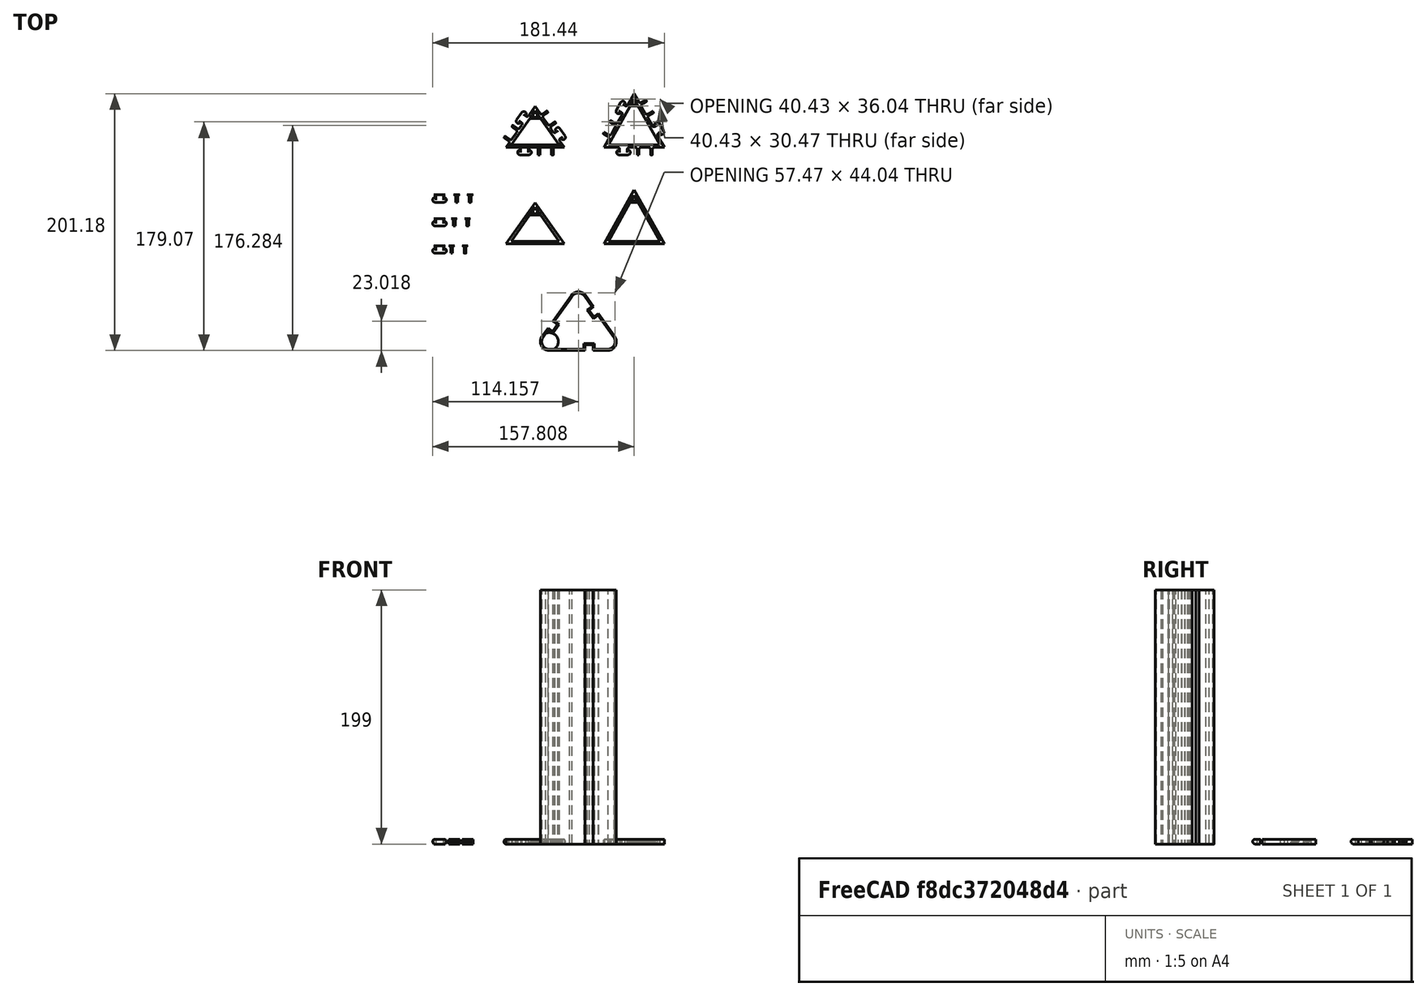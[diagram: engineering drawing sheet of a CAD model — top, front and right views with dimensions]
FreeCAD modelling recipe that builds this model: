
FCSTD DOCUMENT  (FreeCAD 0.20R29177 +233 (Git))
Label: NewGeodesicDome
License: All rights reserved
LicenseURL: http://en.wikipedia.org/wiki/All_rights_reserved
objects: Part::Part2DObjectPython×65, Part::Feature×30, Part::Extrusion×7, Part::MultiFuse×6, Part::Refine×6, Part::Cut×4, Part::FeaturePython×3, App::DocumentObjectGroup×2
note: 121 computed .brp shape members not serialized (recipe doc carries the construction recipe); baked Part::Feature solids carry a one-line shape summary decoded from their .brp

FEATURE [Part::Part2DObjectPython] Line183  label="Line184"  # Draft 2D object (typed FeaturePython)
  ChamferSize = 0
  Closed = false
  End = (88.7449,0.299498,-125.386)
  FilletRadius = 0
  Length = 60.5325
  MakeFace = true
  Placement = pos=(28.2124,0.299498,-125.386) rot=(0,0,1;3.14159rad)
  Points = (2) [(0,0,0),(-60.5325,0,0)]
  Start = (28.2124,0.299498,-125.386)
  Subdivisions = 0
FEATURE [Part::Part2DObjectPython] Line225  label="Line226"  # Draft 2D object (typed FeaturePython)
  ChamferSize = 0
  Closed = false
  End = (58.4771,54.2505,-125.386)
  FilletRadius = 0
  Length = 61.8615
  MakeFace = true
  Placement = pos=(88.7449,0.299498,-125.386) rot=(0,0,1;3.14159rad)
  Points = (2) [(0,0,0),(30.2678,-53.951,0)]
  Start = (88.7449,0.299498,-125.386)
  Subdivisions = 0
FEATURE [Part::Part2DObjectPython] Line175  label="Line186"  # Draft 2D object (typed FeaturePython)
  ChamferSize = 0
  Closed = false
  End = (58.4778,54.2518,-125.386)
  FilletRadius = 0
  Length = 61.8615
  MakeFace = true
  Placement = pos=(28.2124,0.299498,-125.386) rot=(0,0,1;3.14159rad)
  Points = (2) [(0,0,0),(-30.2655,-53.9523,0)]
  Start = (28.2124,0.299498,-125.386)
  Subdivisions = 0
FEATURE [Part::Feature] Cut011001001  label="base-6"
  shape: bbox 47.27 x 42.13 x 3.8 mm, 9 faces (baked)
FEATURE [Part::Part2DObjectPython] Line219  label="Line220"  # Draft 2D object (typed FeaturePython)
  ChamferSize = 0
  Closed = false
  End = (11.2032,0.299498,-125.386)
  FilletRadius = 0
  Length = 52.293
  MakeFace = true
  Placement = pos=(-19.0727,42.9367,-125.386) rot=(0,0,1;3.14159rad)
  Points = (2) [(0,0,0),(-30.2758,42.6372,0)]
  Start = (-19.0727,42.9367,-125.386)
  Subdivisions = 0
FEATURE [Part::Part2DObjectPython] Line217  label="Line218"  # Draft 2D object (typed FeaturePython)
  ChamferSize = 0
  Closed = false
  End = (11.2032,0.299498,-125.386)
  FilletRadius = 0
  Length = 60.5325
  MakeFace = true
  Placement = pos=(-49.3293,0.299498,-125.386) rot=(0,0,1;3.14159rad)
  Points = (2) [(0,0,0),(-60.5325,0,0)]
  Start = (-49.3293,0.299498,-125.386)
  Subdivisions = 0
FEATURE [Part::Part2DObjectPython] Line218  label="Line219"  # Draft 2D object (typed FeaturePython)
  ChamferSize = 0
  Closed = false
  End = (-19.0639,42.9441,-125.386)
  FilletRadius = 0
  Length = 52.293
  MakeFace = true
  Placement = pos=(-49.3293,0.299498,-125.386) rot=(0,0,1;3.14159rad)
  Points = (2) [(0,0,0),(-30.2654,-42.6446,0)]
  Start = (-49.3293,0.299498,-125.386)
  Subdivisions = 0
FEATURE [Part::Feature] Cut011001002001001  label="Base-5"
  shape: bbox 45.49 x 32.04 x 3.8 mm, 9 faces (baked)
FEATURE [Part::Feature] Fusion002009002005002004028003007012002018_solid001001  label="Connector-Father"
  Placement = pos=(-29.7814,0,0) rot=(0,0,1;0rad)
  shape: bbox 10.8 x 5.785 x 3.8 mm, 11 faces (baked)
FEATURE [Part::Feature] Fusion002009002005002004028003007012002019001001  label="Connector-Mother"
  Placement = pos=(-25.7814,0,0) rot=(0,0,1;0rad)
  shape: bbox 15 x 5.785 x 3.8 mm, 19 faces, 2 solids (baked)
FEATURE [Part::Part2DObjectPython] Polygon  # Draft 2D object (typed FeaturePython)
  Area = 9.80568
  ChamferSize = 0
  DrawMode = 0
  FacesNumber = 5
  FilletRadius = 0
  MakeFace = true
  Placement = pos=(-19.0701,29.4211,-127.286) rot=(0.987688,0.156434,0;3.14159rad)
  Radius = 2.03079
FEATURE [Part::Extrusion] Extrusion
  Base = -> Polygon
  Dir = (2.39e-14,-6.7e-14,18.2647)
  DirMode = 0
  FaceMakerClass = Part::FaceMakerBullseye
  LengthFwd = 0
  LengthRev = 0
  Solid = true
  Symmetric = false
FEATURE [Part::Part2DObjectPython] Wire  # Draft 2D object (typed FeaturePython)
  Area = 23.5885
  ChamferSize = 0
  Closed = true
  End = (-17.9137,31.14,-127.286)
  FilletRadius = 0
  Length = 21.5142
  MakeFace = true
  Placement = pos=(-14.8164,26.7782,-127.286) rot=(1,0,0;3.14159rad)
  Points = (4) [(0,0,0),(-8.50437,-3.55271e-15,-1.42109e-14),(-5.40871,-4.36186,0),(-3.09727,-4.36187,7.10543e-14)]
  Start = (-14.8164,26.7782,-127.286)
  Subdivisions = 0
FEATURE [Part::Extrusion] Extrusion001
  Base = -> Wire
  Dir = (6.9e-15,5.4e-15,1.9)
  DirMode = 0
  FaceMakerClass = Part::FaceMakerBullseye
  LengthFwd = 0
  LengthRev = 0
  Solid = true
  Symmetric = false
FEATURE [Part::Part2DObjectPython] Wire001  # Draft 2D object (typed FeaturePython)
  Area = 1.88151
  ChamferSize = 0
  Closed = true
  End = (-17.9137,31.14,-123.486)
  FilletRadius = 0
  Length = 6.30447
  MakeFace = true
  Placement = pos=(-20.2251,31.14,-123.486) rot=(0,0,1;0rad)
  Points = (3) [(0,0,0),(1.15542,1.62801,1.42109e-14),(2.31143,1.92071e-07,-2.84217e-14)]
  Start = (-20.2251,31.14,-123.486)
  Subdivisions = 0
FEATURE [Part::Extrusion] Extrusion002
  Base = -> Wire001
  Dir = (-2.59e-14,4.01e-14,-1.9)
  DirMode = 0
  FaceMakerClass = Part::FaceMakerBullseye
  LengthFwd = 0
  LengthRev = 0
  Solid = true
  Symmetric = false
FEATURE [Part::Cut] Cut
  Base = -> Cut011001002001001
  Tool = -> Extrusion002
FEATURE [Part::MultiFuse] Fusion
  Shapes = -> [Extrusion001,Cut]
FEATURE [Part::Cut] Cut011001002001002
  Base = -> Fusion
  Tool = -> Extrusion
FEATURE [Part::Part2DObjectPython] Polygon002  # Draft 2D object (typed FeaturePython)
  Area = 7.50844
  ChamferSize = 0
  DrawMode = 0
  FacesNumber = 6
  FilletRadius = 0
  MakeFace = true
  Placement = pos=(58.4772,39.1234,-127.286) rot=(1,0,0;3.14159rad)
  Radius = 1.7
FEATURE [Part::Part2DObjectPython] Wire002  # Draft 2D object (typed FeaturePython)
  Area = 1.48683
  ChamferSize = 0
  Closed = true
  End = (59.3905,40.5956,-123.486)
  FilletRadius = 0
  Length = 5.55993
  MakeFace = true
  Placement = pos=(57.564,40.5956,-123.486) rot=(0,0,1;0rad)
  Points = (3) [(0,0,0),(0.913226,1.62801,0),(1.82657,1.51781e-07,0)]
  Start = (57.564,40.5956,-123.486)
  Subdivisions = 0
FEATURE [Part::Extrusion] Extrusion003
  Base = -> Wire002
  Dir = (4e-16,-8e-16,-1.9)
  DirMode = 0
  FaceMakerClass = Part::FaceMakerBullseye
  LengthFwd = 0
  LengthRev = 0
  Solid = true
  Symmetric = false
FEATURE [Part::Cut] Cut011001002001003
  Base = -> Cut011001001
  Tool = -> Extrusion003
FEATURE [Part::Part2DObjectPython] Wire003  # Draft 2D object (typed FeaturePython)
  Area = 15.9332
  ChamferSize = 0
  Closed = true
  End = (55.3513,36.6511,-127.286)
  FilletRadius = 0
  Length = 17.1242
  MakeFace = true
  Placement = pos=(61.6035,36.6511,-127.286) rot=(1,0,0;3.14159rad)
  Points = (4) [(0,0,0),(-2.21293,-3.94449,0),(-4.0395,-3.94449,0),(-6.25215,0,2.84217e-14)]
  Start = (61.6035,36.6511,-127.286)
  Subdivisions = 0
FEATURE [Part::Extrusion] Extrusion004
  Base = -> Wire003
  Dir = (-8.6e-15,-6e-15,1.9)
  DirMode = 0
  FaceMakerClass = Part::FaceMakerBullseye
  LengthFwd = 0
  LengthRev = 0
  Solid = true
  Symmetric = false
FEATURE [Part::Extrusion] Extrusion005
  Base = -> Polygon002
  Dir = (-3.4e-15,6.6e-15,15.6059)
  DirMode = 0
  FaceMakerClass = Part::FaceMakerBullseye
  LengthFwd = 0
  LengthRev = 0
  Solid = true
  Symmetric = false
FEATURE [Part::Cut] Cut011001002001004
  Base = -> Extrusion004
  Tool = -> Extrusion005
FEATURE [Part::MultiFuse] Fusion002009002005002004028003007012002019001002
  Shapes = -> [Cut011001002001004,Cut011001002001003]
FEATURE [Part::Refine] Fusion002009002005002004028003007012002019001002001
  Source = -> Fusion002009002005002004028003007012002019001002
FEATURE [Part::Refine] Cut011001002001002001
  Source = -> Cut011001002001002
FEATURE [Part::Feature] Cut011001002001002001001  label="Base-5angel"
  shape: bbox 45.49 x 32.04 x 3.8 mm, 17 faces (baked)
FEATURE [Part::Feature] Fusion002009002005002004028003007012002019001002001001  label="Base-6angel"
  shape: bbox 47.27 x 42.13 x 3.8 mm, 16 faces (baked)
FEATURE [Part::Part2DObjectPython] Line270  label="Line271"  # Draft 2D object (typed FeaturePython)
  ChamferSize = 0
  Closed = false
  End = (58.4771,129.656,-125.386)
  FilletRadius = 0
  Length = 61.8615
  MakeFace = true
  Placement = pos=(88.7449,75.7054,-125.386) rot=(0,0,1;3.14159rad)
  Points = (2) [(0,0,0),(30.2678,-53.951,0)]
  Start = (88.7449,75.7054,-125.386)
  Subdivisions = 0
FEATURE [Part::Part2DObjectPython] Line271  label="Line272"  # Draft 2D object (typed FeaturePython)
  ChamferSize = 0
  Closed = false
  End = (58.4778,129.658,-125.386)
  FilletRadius = 0
  Length = 61.8615
  MakeFace = true
  Placement = pos=(28.2124,75.7054,-125.386) rot=(0,0,1;3.14159rad)
  Points = (2) [(0,0,0),(-30.2655,-53.9523,0)]
  Start = (28.2124,75.7054,-125.386)
  Subdivisions = 0
FEATURE [Part::Part2DObjectPython] Line272  label="Line273"  # Draft 2D object (typed FeaturePython)
  ChamferSize = 0
  Closed = false
  End = (88.7449,75.7054,-125.386)
  FilletRadius = 0
  Length = 60.5325
  MakeFace = true
  Placement = pos=(28.2124,75.7054,-125.386) rot=(0,0,1;3.14159rad)
  Points = (2) [(0,0,0),(-60.5325,0,0)]
  Start = (28.2124,75.7054,-125.386)
  Subdivisions = 0
FEATURE [Part::Part2DObjectPython] Line273  label="Line274"  # Draft 2D object (typed FeaturePython)
  ChamferSize = 0
  Closed = false
  End = (11.2032,75.7054,-125.386)
  FilletRadius = 0
  Length = 60.5325
  MakeFace = true
  Placement = pos=(-49.3293,75.7054,-125.386) rot=(0,0,1;3.14159rad)
  Points = (2) [(0,0,0),(-60.5325,0,0)]
  Start = (-49.3293,75.7054,-125.386)
  Subdivisions = 0
FEATURE [Part::Part2DObjectPython] Line274  label="Line275"  # Draft 2D object (typed FeaturePython)
  ChamferSize = 0
  Closed = false
  End = (11.2032,75.7054,-125.386)
  FilletRadius = 0
  Length = 52.293
  MakeFace = true
  Placement = pos=(-19.0727,118.343,-125.386) rot=(0,0,1;3.14159rad)
  Points = (2) [(0,0,0),(-30.2758,42.6372,0)]
  Start = (-19.0727,118.343,-125.386)
  Subdivisions = 0
FEATURE [Part::Part2DObjectPython] Line275  label="Line276"  # Draft 2D object (typed FeaturePython)
  ChamferSize = 0
  Closed = false
  End = (-19.0639,118.35,-125.386)
  FilletRadius = 0
  Length = 52.293
  MakeFace = true
  Placement = pos=(-49.3293,75.7054,-125.386) rot=(0,0,1;3.14159rad)
  Points = (2) [(0,0,0),(-30.2654,-42.6446,0)]
  Start = (-49.3293,75.7054,-125.386)
  Subdivisions = 0
FEATURE [Part::Feature] Fusion002009002005002004028003007012002019001002001002  label="Base-6angel001"
  Placement = pos=(0,75.4059,-2.8e-14) rot=(0,0,1;0rad)
  shape: bbox 47.27 x 42.13 x 3.8 mm, 16 faces (baked)
FEATURE [Part::Feature] Cut011001002001002001002  label="Base-5angel001"
  Placement = pos=(0,75.4059,-2.8e-14) rot=(0,0,1;0rad)
  shape: bbox 45.49 x 32.04 x 3.8 mm, 17 faces (baked)
FEATURE [Part::Part2DObjectPython] Line276  label="Line277"  # Draft 2D object (typed FeaturePython)
  Area = 0
  ChamferSize = 0
  Closed = false
  End = (-75.2318,29.5332,-125.386)
  FilletRadius = 0
  Length = 9.03897
  MakeFace = true
  Placement = pos=(-75.2318,38.5722,-125.386) rot=(1,0,0;3.14159rad)
  Points = (2) [(0,0,0),(0,9.03897,0)]
  Start = (-75.2318,38.5722,-125.386)
  Subdivisions = 0
FEATURE [Part::Part2DObjectPython] Line277  label="Line278"  # Draft 2D object (typed FeaturePython)
  Area = 0
  ChamferSize = 0
  Closed = false
  End = (-93.9318,29.5332,-125.386)
  FilletRadius = 0
  Length = 8.13178
  MakeFace = true
  Placement = pos=(-93.9318,37.665,-125.386) rot=(1,0,0;3.14159rad)
  Points = (2) [(0,0,0),(0,8.13178,0)]
  Start = (-93.9318,37.665,-125.386)
  Subdivisions = 0
FEATURE [Part::Part2DObjectPython] Line278  label="Line279"  # Draft 2D object (typed FeaturePython)
  Area = 0
  ChamferSize = 0
  Closed = false
  End = (-104.082,38.5722,-125.386)
  FilletRadius = 0
  Length = 35
  MakeFace = true
  Placement = pos=(-69.0818,38.5722,-125.386) rot=(1,0,0;3.14159rad)
  Points = (2) [(0,0,0),(-35,0,0)]
  Start = (-69.0818,38.5722,-125.386)
  Subdivisions = 0
FEATURE [Part::Part2DObjectPython] Line279  label="Line280"  # Draft 2D object (typed FeaturePython)
  Area = 0
  ChamferSize = 0
  Closed = false
  End = (-84.5818,42.4571,-125.386)
  FilletRadius = 0
  Length = 12.9238
  MakeFace = true
  Placement = pos=(-84.5818,29.5332,-125.386) rot=(1,0,0;3.14159rad)
  Points = (2) [(0,0,0),(8.10019e-13,-12.9238,-1.42109e-14)]
  Start = (-84.5818,29.5332,-125.386)
  Subdivisions = 0
FEATURE [Part::Feature] Fusion002009002005002004028003007012002018_solid001002  label="Connector-Father001"
  Placement = pos=(-29.7814,-18.5719,0) rot=(0,0,1;0rad)
  shape: bbox 10.8 x 5.785 x 3.8 mm, 11 faces (baked)
FEATURE [Part::Feature] Fusion002009002005002004028003007012002019001002001003  label="Connector-Mother001"
  Placement = pos=(-27.7814,-18.5719,0) rot=(0,0,1;0rad)
  shape: bbox 15 x 5.785 x 3.8 mm, 19 faces, 2 solids (baked)
FEATURE [Part::Part2DObjectPython] Line280  label="Line281"  # Draft 2D object (typed FeaturePython)
  Area = 0
  ChamferSize = 0
  Closed = false
  End = (-77.2318,10.9613,-125.386)
  FilletRadius = 0
  Length = 9.03897
  MakeFace = true
  Placement = pos=(-77.2318,20.0003,-125.386) rot=(1,0,0;3.14159rad)
  Points = (2) [(0,0,0),(0,9.03897,0)]
  Start = (-77.2318,20.0003,-125.386)
  Subdivisions = 0
FEATURE [Part::Part2DObjectPython] Line281  label="Line282"  # Draft 2D object (typed FeaturePython)
  Area = 0
  ChamferSize = 0
  Closed = false
  End = (-93.9318,10.9613,-125.386)
  FilletRadius = 0
  Length = 8.13178
  MakeFace = true
  Placement = pos=(-93.9318,19.0931,-125.386) rot=(1,0,0;3.14159rad)
  Points = (2) [(0,0,0),(0,8.13178,0)]
  Start = (-93.9318,19.0931,-125.386)
  Subdivisions = 0
FEATURE [Part::Part2DObjectPython] Line282  label="Line283"  # Draft 2D object (typed FeaturePython)
  Area = 0
  ChamferSize = 0
  Closed = false
  End = (-104.082,20.0003,-125.386)
  FilletRadius = 0
  Length = 35
  MakeFace = true
  Placement = pos=(-69.0818,20.0003,-125.386) rot=(1,0,0;3.14159rad)
  Points = (2) [(0,0,0),(-35,0,0)]
  Start = (-69.0818,20.0003,-125.386)
  Subdivisions = 0
FEATURE [Part::Part2DObjectPython] Line283  label="Line284"  # Draft 2D object (typed FeaturePython)
  Area = 0
  ChamferSize = 0
  Closed = false
  End = (-85.5818,23.8851,-125.386)
  FilletRadius = 0
  Length = 12.9238
  MakeFace = true
  Placement = pos=(-85.5818,10.9613,-125.386) rot=(1,0,0;3.14159rad)
  Points = (2) [(0,0,0),(8.10019e-13,-12.9238,-1.42109e-14)]
  Start = (-85.5818,10.9613,-125.386)
  Subdivisions = 0
FEATURE [Part::Feature] Fusion002009002005002004028003007012002018_solid001003  label="Connector-Father002"
  Placement = pos=(-29.7814,-39.9,0) rot=(0,0,1;0rad)
  shape: bbox 10.8 x 5.785 x 3.8 mm, 11 faces (baked)
FEATURE [Part::Feature] Fusion002009002005002004028003007012002019001002001004  label="Connector-Mother002"
  Placement = pos=(-29.7814,-39.9,0) rot=(0,0,1;0rad)
  shape: bbox 15 x 5.785 x 3.8 mm, 19 faces, 2 solids (baked)
FEATURE [Part::Part2DObjectPython] Line285  label="Line286"  # Draft 2D object (typed FeaturePython)
  Area = 0
  ChamferSize = 0
  Closed = false
  End = (-79.2318,-10.3668,-125.386)
  FilletRadius = 0
  Length = 9.03897
  MakeFace = true
  Placement = pos=(-79.2318,-1.32783,-125.386) rot=(1,0,0;3.14159rad)
  Points = (2) [(0,0,0),(0,9.03897,0)]
  Start = (-79.2318,-1.32783,-125.386)
  Subdivisions = 0
FEATURE [Part::Part2DObjectPython] Line286  label="Line287"  # Draft 2D object (typed FeaturePython)
  Area = 0
  ChamferSize = 0
  Closed = false
  End = (-93.9318,-10.3668,-125.386)
  FilletRadius = 0
  Length = 8.13178
  MakeFace = true
  Placement = pos=(-93.9318,-2.23501,-125.386) rot=(1,0,0;3.14159rad)
  Points = (2) [(0,0,0),(0,8.13178,0)]
  Start = (-93.9318,-2.23501,-125.386)
  Subdivisions = 0
FEATURE [Part::Part2DObjectPython] Line287  label="Line288"  # Draft 2D object (typed FeaturePython)
  Area = 0
  ChamferSize = 0
  Closed = false
  End = (-104.082,-1.32783,-125.386)
  FilletRadius = 0
  Length = 35
  MakeFace = true
  Placement = pos=(-69.0818,-1.32783,-125.386) rot=(1,0,0;3.14159rad)
  Points = (2) [(0,0,0),(-35,0,0)]
  Start = (-69.0818,-1.32783,-125.386)
  Subdivisions = 0
FEATURE [Part::Part2DObjectPython] Line288  label="Line289"  # Draft 2D object (typed FeaturePython)
  Area = 0
  ChamferSize = 0
  Closed = false
  End = (-86.5818,2.55704,-125.386)
  FilletRadius = 0
  Length = 12.9238
  MakeFace = true
  Placement = pos=(-86.5818,-10.3668,-125.386) rot=(1,0,0;3.14159rad)
  Points = (2) [(0,0,0),(8.10019e-13,-12.9238,-1.42109e-14)]
  Start = (-86.5818,-10.3668,-125.386)
  Subdivisions = 0
FEATURE [Part::Part2DObjectPython] Line  # Draft 2D object (typed FeaturePython)
  Area = 0
  ChamferSize = 0
  Closed = false
  End = (-80.2318,23.8851,-127.286)
  FilletRadius = 0
  Length = 2
  MakeFace = true
  Placement = pos=(-82.2318,23.8851,-127.286) rot=(1,0,0;3.14159rad)
  Points = (2) [(0,0,0),(2,0,0)]
  Start = (-82.2318,23.8851,-127.286)
  Subdivisions = 0
FEATURE [Part::Feature] Fusion002009002005002004028003007012002018_solid001004  label="Connector-Father003"
  Placement = pos=(-98.5261,73.0316,-2.42e-13) rot=(0,0,1;4.09518rad)
  shape: bbox 9.698 x 10.67 x 3.8 mm, 11 faces (baked)
FEATURE [Part::Feature] Fusion002009002005002004028003007012002019001002001005  label="Connector-Mother003"
  Placement = pos=(-98.5261,73.0316,-2.42e-13) rot=(0,0,1;4.09518rad)
  shape: bbox 12.53 x 14.36 x 3.8 mm, 19 faces, 2 solids (baked)
FEATURE [Part::Part2DObjectPython] Line291  label="Line292"  # Draft 2D object (typed FeaturePython)
  Area = 0
  ChamferSize = 0
  Closed = false
  End = (-24.0682,111.299,-125.386)
  FilletRadius = 0
  Length = 35
  MakeFace = true
  Placement = pos=(-44.325,82.7566,-125.386) rot=(-0.45893,0.888472,0;3.14159rad)
  Points = (2) [(0,0,0),(-35,1.13687e-13,0)]
  Start = (-44.325,82.7566,-125.386)
  Subdivisions = 0
FEATURE [Part::Part2DObjectPython] Line292  label="Line293"  # Draft 2D object (typed FeaturePython)
  Area = 0
  ChamferSize = 0
  Closed = false
  End = (-37.3139,108.253,-125.386)
  FilletRadius = 0
  Length = 8.13178
  MakeFace = true
  Placement = pos=(-30.6825,103.547,-125.386) rot=(-0.45893,0.888472,0;3.14159rad)
  Points = (2) [(0,0,0),(5.68434e-14,8.13178,0)]
  Start = (-30.6825,103.547,-125.386)
  Subdivisions = 0
FEATURE [Part::Part2DObjectPython] Line293  label="Line294"  # Draft 2D object (typed FeaturePython)
  Area = 0
  ChamferSize = 0
  Closed = false
  End = (-31.0286,94.7793,-125.386)
  FilletRadius = 0
  Length = 12.9238
  MakeFace = true
  Placement = pos=(-41.5679,102.259,-125.386) rot=(-0.45893,0.888472,0;3.14159rad)
  Points = (2) [(0,0,0),(8.10019e-13,-12.9238,-1.42109e-14)]
  Start = (-41.5679,102.259,-125.386)
  Subdivisions = 0
FEATURE [Part::Part2DObjectPython] Line294  label="Line295"  # Draft 2D object (typed FeaturePython)
  Area = 0
  ChamferSize = 0
  Closed = false
  End = (-45.8218,96.2653,-125.386)
  FilletRadius = 0
  Length = 9.03897
  MakeFace = true
  Placement = pos=(-38.4506,91.0338,-125.386) rot=(-0.45893,0.888472,0;3.14159rad)
  Points = (2) [(0,0,0),(0,9.03897,0)]
  Start = (-38.4506,91.0338,-125.386)
  Subdivisions = 0
FEATURE [Part::Feature] Fusion002009002005002004028003007012002018_solid001005  label="Connector-Father004"
  Placement = pos=(-4.9284,165.046,-2.42e-13) rot=(0,0,1;2.18826rad)
  shape: bbox 9.699 x 10.67 x 3.8 mm, 11 faces (baked)
FEATURE [Part::Feature] Fusion002009002005002004028003007012002019001002001006  label="Connector-Mother004"
  Placement = pos=(-4.9284,165.046,-2.42e-13) rot=(0,0,1;2.18826rad)
  shape: bbox 12.53 x 14.36 x 3.8 mm, 19 faces, 2 solids (baked)
FEATURE [Part::Part2DObjectPython] Line295  label="Line296"  # Draft 2D object (typed FeaturePython)
  Area = 0
  ChamferSize = 0
  Closed = false
  End = (8.13245,95.6421,-125.386)
  FilletRadius = 0
  Length = 8.13178
  MakeFace = true
  Placement = pos=(1.50218,90.9341,-125.386) rot=(0.458822,0.888528,0;3.14159rad)
  Points = (2) [(0,0,0),(4.26326e-14,8.13178,0)]
  Start = (1.50218,90.9341,-125.386)
  Subdivisions = 0
FEATURE [Part::Part2DObjectPython] Line296  label="Line297"  # Draft 2D object (typed FeaturePython)
  Area = 0
  ChamferSize = 0
  Closed = false
  End = (-6.66042,94.1525,-125.386)
  FilletRadius = 0
  Length = 12.9238
  MakeFace = true
  Placement = pos=(3.87705,101.635,-125.386) rot=(0.458822,0.888528,0;3.14159rad)
  Points = (2) [(0,0,0),(7.81597e-13,-12.9238,-1.42109e-14)]
  Start = (3.87705,101.635,-125.386)
  Subdivisions = 0
FEATURE [Part::Part2DObjectPython] Line297  label="Line298"  # Draft 2D object (typed FeaturePython)
  Area = 0
  ChamferSize = 0
  Closed = false
  End = (-0.378342,107.628,-125.386)
  FilletRadius = 0
  Length = 9.03897
  MakeFace = true
  Placement = pos=(-7.74828,102.395,-125.386) rot=(0.458822,0.888528,0;3.14159rad)
  Points = (2) [(0,0,0),(1.42109e-14,9.03897,0)]
  Start = (-7.74828,102.395,-125.386)
  Subdivisions = 0
FEATURE [Part::Part2DObjectPython] Line298  label="Line299"  # Draft 2D object (typed FeaturePython)
  Area = 0
  ChamferSize = 0
  Closed = false
  End = (6.63901,82.1331,-125.386)
  FilletRadius = 0
  Length = 35
  MakeFace = true
  Placement = pos=(-13.6248,110.67,-125.386) rot=(0.458822,0.888528,0;3.14159rad)
  Points = (2) [(0,0,0),(-35,-7.10543e-15,0)]
  Start = (-13.6248,110.67,-125.386)
  Subdivisions = 0
FEATURE [Part::Feature] Fusion002009002005002004028003007012002018_solid001006  label="Connector-Father005"
  Placement = pos=(36.7373,37.1332,-2.42e-13) rot=(0,0,1;0rad)
  shape: bbox 10.8 x 5.785 x 3.8 mm, 11 faces (baked)
FEATURE [Part::Part2DObjectPython] Line299  label="Line300"  # Draft 2D object (typed FeaturePython)
  Area = 0
  ChamferSize = 0
  Closed = false
  End = (-37.5631,75.7054,-125.386)
  FilletRadius = 0
  Length = 35
  MakeFace = true
  Placement = pos=(-2.56309,75.7054,-125.386) rot=(1,0,0;3.14159rad)
  Points = (2) [(0,0,0),(-35,0,0)]
  Start = (-2.56309,75.7054,-125.386)
  Subdivisions = 0
FEATURE [Part::Part2DObjectPython] Line300  label="Line301"  # Draft 2D object (typed FeaturePython)
  Area = 0
  ChamferSize = 0
  Closed = false
  End = (-10.7131,66.6664,-125.386)
  FilletRadius = 0
  Length = 9.03897
  MakeFace = true
  Placement = pos=(-10.7131,75.7054,-125.386) rot=(1,0,0;3.14159rad)
  Points = (2) [(0,0,0),(0,9.03897,0)]
  Start = (-10.7131,75.7054,-125.386)
  Subdivisions = 0
FEATURE [Part::Part2DObjectPython] Line301  label="Line302"  # Draft 2D object (typed FeaturePython)
  Area = 0
  ChamferSize = 0
  Closed = false
  End = (-19.0631,79.5903,-125.386)
  FilletRadius = 0
  Length = 12.9238
  MakeFace = true
  Placement = pos=(-19.0631,66.6664,-125.386) rot=(1,0,0;3.14159rad)
  Points = (2) [(0,0,0),(8.10019e-13,-12.9238,-1.42109e-14)]
  Start = (-19.0631,66.6664,-125.386)
  Subdivisions = 0
FEATURE [Part::Part2DObjectPython] Line302  label="Line303"  # Draft 2D object (typed FeaturePython)
  Area = 0
  ChamferSize = 0
  Closed = false
  End = (-27.4131,66.6664,-125.386)
  FilletRadius = 0
  Length = 8.13178
  MakeFace = true
  Placement = pos=(-27.4131,74.7982,-125.386) rot=(1,0,0;3.14159rad)
  Points = (2) [(0,0,0),(0,8.13178,0)]
  Start = (-27.4131,74.7982,-125.386)
  Subdivisions = 0
FEATURE [Part::Feature] Fusion002009002005002004028003007012002018_solid001007  label="Connector-Father006"
  Placement = pos=(114.279,37.1332,-8.669e-13) rot=(0,0,1;0rad)
  shape: bbox 10.8 x 5.785 x 3.8 mm, 11 faces (baked)
FEATURE [Part::Feature] Fusion002009002005002004028003007012002019001002001008  label="Connector-Mother006"
  Placement = pos=(116.279,37.1332,-8.669e-13) rot=(0,0,1;0rad)
  shape: bbox 15 x 5.785 x 3.8 mm, 19 faces, 2 solids (baked)
FEATURE [Part::Part2DObjectPython] Line303  label="Line304"  # Draft 2D object (typed FeaturePython)
  Area = 0
  ChamferSize = 0
  Closed = false
  End = (39.9786,75.7054,-125.386)
  FilletRadius = 0
  Length = 35
  MakeFace = true
  Placement = pos=(74.9786,75.7054,-125.386) rot=(1,0,0;3.14159rad)
  Points = (2) [(0,0,0),(-35,0,0)]
  Start = (74.9786,75.7054,-125.386)
  Subdivisions = 0
FEATURE [Part::Part2DObjectPython] Line304  label="Line305"  # Draft 2D object (typed FeaturePython)
  Area = 0
  ChamferSize = 0
  Closed = false
  End = (66.8286,66.6664,-125.386)
  FilletRadius = 0
  Length = 9.03897
  MakeFace = true
  Placement = pos=(66.8286,75.7054,-125.386) rot=(1,0,0;3.14159rad)
  Points = (2) [(0,0,0),(0,9.03897,0)]
  Start = (66.8286,75.7054,-125.386)
  Subdivisions = 0
FEATURE [Part::Part2DObjectPython] Line305  label="Line306"  # Draft 2D object (typed FeaturePython)
  Area = 0
  ChamferSize = 0
  Closed = false
  End = (58.4786,79.5903,-125.386)
  FilletRadius = 0
  Length = 12.9238
  MakeFace = true
  Placement = pos=(58.4786,66.6664,-125.386) rot=(1,0,0;3.14159rad)
  Points = (2) [(0,0,0),(8.10019e-13,-12.9238,-1.42109e-14)]
  Start = (58.4786,66.6664,-125.386)
  Subdivisions = 0
FEATURE [Part::Part2DObjectPython] Line306  label="Line307"  # Draft 2D object (typed FeaturePython)
  Area = 0
  ChamferSize = 0
  Closed = false
  End = (50.1286,66.6664,-125.386)
  FilletRadius = 0
  Length = 8.13178
  MakeFace = true
  Placement = pos=(50.1286,74.7982,-125.386) rot=(1,0,0;3.14159rad)
  Points = (2) [(0,0,0),(0,8.13178,0)]
  Start = (50.1286,74.7982,-125.386)
  Subdivisions = 0
FEATURE [Part::Feature] Fusion002009002005002004028003007012002018_solid001008  label="Connector-Father007"
  Placement = pos=(-17.1063,73.7589,-2.56e-13) rot=(0,0,-1;2.08202rad)
  shape: bbox 9.202 x 10.78 x 3.8 mm, 11 faces (baked)
FEATURE [Part::Feature] Fusion002009002005002004028003007012002019001002001009  label="Connector-Mother007"
  Placement = pos=(-19.0633,70.2703,-2.56e-13) rot=(0,0,-1;2.08202rad)
  shape: bbox 11.65 x 14.6 x 3.8 mm, 19 faces, 2 solids (baked)
FEATURE [Part::Part2DObjectPython] Line307  label="Line308"  # Draft 2D object (typed FeaturePython)
  Area = 0
  ChamferSize = 0
  Closed = false
  End = (52.8854,119.688,-125.386)
  FilletRadius = 0
  Length = 35
  MakeFace = true
  Placement = pos=(35.7618,89.1633,-125.386) rot=(-0.505349,0.862915,0;3.14159rad)
  Points = (2) [(0,0,0),(-35,0,0)]
  Start = (35.7618,89.1633,-125.386)
  Subdivisions = 0
FEATURE [Part::Part2DObjectPython] Line308  label="Line309"  # Draft 2D object (typed FeaturePython)
  Area = 0
  ChamferSize = 0
  Closed = false
  End = (46.7332,100.781,-125.386)
  FilletRadius = 0
  Length = 12.9238
  MakeFace = true
  Placement = pos=(35.4618,107.104,-125.386) rot=(-0.505349,0.862915,0;3.14159rad)
  Points = (2) [(0,0,0),(7.53175e-13,-12.9238,-1.42109e-14)]
  Start = (35.4618,107.104,-125.386)
  Subdivisions = 0
FEATURE [Part::Part2DObjectPython] Line309  label="Line310"  # Draft 2D object (typed FeaturePython)
  Area = 0
  ChamferSize = 0
  Closed = false
  End = (40.0362,115.258,-125.386)
  FilletRadius = 0
  Length = 8.13178
  MakeFace = true
  Placement = pos=(47.1283,111.28,-125.386) rot=(-0.505349,0.862915,0;3.14159rad)
  Points = (2) [(0,0,0),(-1.42109e-14,8.13178,0)]
  Start = (47.1283,111.28,-125.386)
  Subdivisions = 0
FEATURE [Part::Part2DObjectPython] Line310  label="Line311"  # Draft 2D object (typed FeaturePython)
  Area = 0
  ChamferSize = 0
  Closed = false
  End = (30.8873,98.9492,-125.386)
  FilletRadius = 0
  Length = 9.03897
  MakeFace = true
  Placement = pos=(38.7706,94.527,-125.386) rot=(-0.505349,0.862915,0;3.14159rad)
  Points = (2) [(0,0,0),(-1.42109e-14,9.03897,0)]
  Start = (38.7706,94.527,-125.386)
  Subdivisions = 0
FEATURE [Part::Feature] Fusion002009002005002004028003007012002018_solid001009  label="Connector-Father008"
  Placement = pos=(80.4379,169.346,-8.67e-13) rot=(0,0,1;2.08206rad)
  shape: bbox 9.202 x 10.78 x 3.8 mm, 11 faces (baked)
FEATURE [Part::Feature] Fusion002009002005002004028003007012002019001002001010  label="Connector-Mother008"
  Placement = pos=(78.4807,172.835,-8.67e-13) rot=(0,0,1;2.08206rad)
  shape: bbox 11.65 x 14.6 x 3.8 mm, 19 faces, 2 solids (baked)
FEATURE [Part::Part2DObjectPython] Line311  label="Line312"  # Draft 2D object (typed FeaturePython)
  Area = 0
  ChamferSize = 0
  Closed = false
  End = (83.152,85.6744,-125.386)
  FilletRadius = 0
  Length = 35
  MakeFace = true
  Placement = pos=(66.0271,116.199,-125.386) rot=(0.50533,0.862926,0;3.14159rad)
  Points = (2) [(0,0,0),(-35,2.84217e-14,0)]
  Start = (66.0271,116.199,-125.386)
  Subdivisions = 0
FEATURE [Part::Part2DObjectPython] Line312  label="Line313"  # Draft 2D object (typed FeaturePython)
  Area = 0
  ChamferSize = 0
  Closed = false
  End = (76.9193,115.258,-125.386)
  FilletRadius = 0
  Length = 9.03897
  MakeFace = true
  Placement = pos=(69.0362,110.835,-125.386) rot=(0.50533,0.862926,0;3.14159rad)
  Points = (2) [(0,0,0),(1.42109e-14,9.03897,0)]
  Start = (69.0362,110.835,-125.386)
  Subdivisions = 0
FEATURE [Part::Part2DObjectPython] Line313  label="Line314"  # Draft 2D object (typed FeaturePython)
  Area = 0
  ChamferSize = 0
  Closed = false
  End = (70.2229,100.78,-125.386)
  FilletRadius = 0
  Length = 12.9238
  MakeFace = true
  Placement = pos=(81.4941,107.103,-125.386) rot=(0.50533,0.862926,0;3.14159rad)
  Points = (2) [(0,0,0),(7.95808e-13,-12.9238,-1.42109e-14)]
  Start = (81.4941,107.103,-125.386)
  Subdivisions = 0
FEATURE [Part::Part2DObjectPython] Line314  label="Line315"  # Draft 2D object (typed FeaturePython)
  Area = 0
  ChamferSize = 0
  Closed = false
  End = (86.0689,98.9491,-125.386)
  FilletRadius = 0
  Length = 8.13178
  MakeFace = true
  Placement = pos=(78.9769,94.9704,-125.386) rot=(0.50533,0.862926,0;3.14159rad)
  Points = (2) [(0,0,0),(0,8.13178,0)]
  Start = (78.9769,94.9704,-125.386)
  Subdivisions = 0
FEATURE [Part::MultiFuse] Fusion002009002005002004028003007012002019001002001012
  Shapes = -> [Fusion002009002005002004028003007012002019001002001002,Fusion002009002005002004028003007012002018_solid001007,Fusion002009002005002004028003007012002019001002001008,Fusion002009002005002004028003007012002019001002001009,Fusion002009002005002004028003007012002018_solid001008,Fusion002009002005002004028003007012002019001002001010,Fusion002009002005002004028003007012002018_solid001009]
FEATURE [Part::Feature] Fusion002009002005002004028003007012002019001002001011_solid  label="Fusion002009002005002004028003007012002019001002001011 (Solid)"
  shape: bbox 52.48 x 42.14 x 8.116 mm, 109 faces (baked)
FEATURE [Part::Refine] Fusion002009002005002004028003007012002019001002001011_solid001  label="Fusion002009002005002004028003007012002019001002001011 (Solid)001"
  Source = -> Fusion002009002005002004028003007012002019001002001011_solid
FEATURE [Part::Feature] Fusion002009002005002004028003007012002019001002001011_solid001001  label="5AnglePart"
  shape: bbox 48.16 x 37.82 x 3.8 mm, 89 faces (baked)
FEATURE [Part::Feature] Fusion002009002005002004028003007012002019001002001012_solid  label="Fusion002009002005002004028003007012002019001002001012 (Solid)"
  shape: bbox 47.93 x 47.91 x 3.8 mm, 124 faces (baked)
FEATURE [Part::Refine] Fusion002009002005002004028003007012002019001002001012_solid001  label="Fusion002009002005002004028003007012002019001002001012 (Solid)001"
  Source = -> Fusion002009002005002004028003007012002019001002001012_solid
FEATURE [Part::Feature] Fusion002009002005002004028003007012002019001002001012_solid001001  label="6AnglePart"
  shape: bbox 47.93 x 47.91 x 3.8 mm, 88 faces (baked)
FEATURE [Part::Part2DObjectPython] Rectangle  # Draft 2D object (typed FeaturePython)
  Area = 4221.28
  ChamferSize = 0
  Columns = 1
  FilletRadius = 0
  Height = 63.5218
  Length = 66.454
  MakeFace = true
  Placement = pos=(15.1652,81.5903,-154.872) rot=(0,0.707107,0.707107;3.14159rad)
  Rows = 1
FEATURE [Part::FeaturePython] Slice  # WARN: FeaturePython — macro-defined, semantics opaque (R4)
  Base = -> Cut011001002001002001002
  Mode = 1
  Tolerance = 0
  Tools = -> [Rectangle]
FEATURE [Part::FeaturePython] Slice_child0  label="Slice.0"  # WARN: FeaturePython — macro-defined, semantics opaque (R4)
  Base = -> Slice
  FilterType = 1
  Invert = false
  OverrideMaxVal = 0
  WindowFrom = 80
  WindowTo = 100
  items = 0
FEATURE [Part::FeaturePython] Slice_child1  label="Slice.1"  # WARN: FeaturePython — macro-defined, semantics opaque (R4)
  Base = -> Slice
  FilterType = 1
  Invert = false
  OverrideMaxVal = 0
  WindowFrom = 80
  WindowTo = 100
  items = 1
FEATURE [Part::Part2DObjectPython] Wire004  # Draft 2D object (typed FeaturePython)
  Area = 88.1371
  ChamferSize = 0
  Closed = true
  End = (3.67995,79.5903,-123.486)
  FilletRadius = 0
  Length = 93.0425
  MakeFace = true
  Placement = pos=(-41.8084,79.5903,-123.486) rot=(0,0.707107,0.707107;3.14159rad)
  Points = (4) [(0,0,0),(-1.41942,0,2),(-44.0682,-2.84217e-14,2),(-45.4883,-1.42109e-14,-2.84217e-14)]
  Start = (-41.8084,79.5903,-123.486)
  Subdivisions = 0
FEATURE [Part::Extrusion] Extrusion006
  Base = -> Wire004
  Dir = (-4.5e-15,8.4e-15,-3.8)
  DirMode = 0
  FaceMakerClass = Part::FaceMakerBullseye
  LengthFwd = 0
  LengthRev = 0
  Solid = true
  Symmetric = false
FEATURE [Part::MultiFuse] Fusion002009002005002004028003007012002019001002001013
  Shapes = -> [Slice_child1,Slice_child0]
FEATURE [App::DocumentObjectGroup] GrExplode_Slice  label="Exploded Slice"
  Group = -> [Fusion002009002005002004028003007012002019001002001013]
FEATURE [Part::Refine] Fusion002009002005002004028003007012002019001002001013001
  Source = -> Fusion002009002005002004028003007012002019001002001013
FEATURE [Part::Feature] Fusion002009002005002004028003007012002019001002001013002  label="Connector-Mother009"
  Placement = pos=(38.7373,37.1332,-2.42e-13) rot=(0,0,1;0rad)
  shape: bbox 18.28 x 9.069 x 7.084 mm, 19 faces, 2 solids (baked)
FEATURE [Part::Part2DObjectPython] Line318  label="Line319"  # Draft 2D object (typed FeaturePython)
  Area = 0
  ChamferSize = 0
  Closed = false
  End = (-10.7131,66.6664,-125.386)
  FilletRadius = 0
  Length = 9.03897
  MakeFace = true
  Placement = pos=(-10.7131,75.7054,-125.386) rot=(1,0,0;3.14159rad)
  Points = (2) [(0,0,0),(0,9.03897,0)]
  Start = (-10.7131,75.7054,-125.386)
  Subdivisions = 0
FEATURE [Part::MultiFuse] Fusion002009002005002004028003007012002019001002001013003
  Shapes = -> [Fusion002009002005002004028003007012002019001002001013001,Fusion002009002005002004028003007012002019001002001013002]
FEATURE [Part::MultiFuse] Fusion002009002005002004028003007012002019001002001013004
  Shapes = -> [Fusion002009002005002004028003007012002019001002001013003,Fusion002009002005002004028003007012002018_solid001006,Fusion002009002005002004028003007012002018_solid001005,Fusion002009002005002004028003007012002018_solid001004,Fusion002009002005002004028003007012002019001002001005,Fusion002009002005002004028003007012002019001002001006]
FEATURE [Part::Refine] Fusion002009002005002004028003007012002019001002001013004001
  Source = -> Fusion002009002005002004028003007012002019001002001013004
FEATURE [Part::Part2DObjectPython] Line317  label="Line318"  # Draft 2D object (typed FeaturePython)
  Area = 0
  ChamferSize = 0
  Closed = false
  End = (-39.5631,75.7054,-125.386)
  FilletRadius = 0
  Length = 35
  MakeFace = true
  Placement = pos=(-4.56309,75.7054,-125.386) rot=(1,0,0;3.14159rad)
  Points = (2) [(0,0,0),(-35,0,0)]
  Start = (-4.56309,75.7054,-125.386)
  Subdivisions = 0
FEATURE [Part::Part2DObjectPython] Line322  label="Line323"  # Draft 2D object (typed FeaturePython)
  Area = 0
  ChamferSize = 0
  Closed = false
  End = (14.8792,73.8102,-125.386)
  FilletRadius = 0
  Length = 58.64
  MakeFace = true
  Placement = pos=(-19.0713,121.622,-125.386) rot=(-0.807496,-0.417103,0.417103;1.783rad)
  Points = (2) [(0,0,0),(-19.3412,2.13163e-12,-55.3585)]
  Start = (-19.0713,121.622,-125.386)
  Subdivisions = 0
FEATURE [Part::Part2DObjectPython] Line323  label="Line324"  # Draft 2D object (typed FeaturePython)
  Area = 0
  ChamferSize = 0
  Closed = false
  End = (-53.0077,73.8054,-125.386)
  FilletRadius = 0
  Length = 67.8869
  MakeFace = true
  Placement = pos=(14.8792,73.8102,-125.386) rot=(-0.807496,-0.417103,0.417103;1.783rad)
  Points = (2) [(0,0,0),(-39.2945,-1.20792e-12,55.3585)]
  Start = (14.8792,73.8102,-125.386)
  Subdivisions = 0
FEATURE [Part::Part2DObjectPython] Line324  label="Line325"  # Draft 2D object (typed FeaturePython)
  Area = 0
  ChamferSize = 0
  Closed = false
  End = (-19.0713,121.622,-125.386)
  FilletRadius = 0
  Length = 58.6357
  MakeFace = true
  Placement = pos=(-53.0077,73.8054,-125.386) rot=(-0.807496,-0.417103,0.417103;1.783rad)
  Points = (2) [(0,0,0),(58.6357,-2.40163e-12,1.42109e-14)]
  Start = (-53.0077,73.8054,-125.386)
  Subdivisions = 0
FEATURE [Part::Part2DObjectPython] Line328  label="Line329"  # Draft 2D object (typed FeaturePython)
  Area = 0
  ChamferSize = 0
  Closed = false
  End = (24.9693,73.813,-125.386)
  FilletRadius = 0
  Length = 68.4874
  MakeFace = true
  Placement = pos=(58.4755,133.545,-125.386) rot=(1,0,0;3.14159rad)
  Points = (2) [(0,0,0),(-33.5062,59.7316,0)]
  Start = (58.4755,133.545,-125.386)
  Subdivisions = 0
FEATURE [Part::Part2DObjectPython] Line329  label="Line330"  # Draft 2D object (typed FeaturePython)
  Area = 0
  ChamferSize = 0
  Closed = false
  End = (92.0028,73.817,-125.386)
  FilletRadius = 0
  Length = 68.4942
  MakeFace = true
  Placement = pos=(58.4755,133.545,-125.386) rot=(1,0,0;3.14159rad)
  Points = (2) [(0,0,0),(33.5273,59.7275,1.42109e-14)]
  Start = (58.4755,133.545,-125.386)
  Subdivisions = 0
FEATURE [Part::Part2DObjectPython] Line330  label="Line331"  # Draft 2D object (typed FeaturePython)
  Area = 0
  ChamferSize = 0
  Closed = false
  End = (24.9693,73.813,-125.386)
  FilletRadius = 0
  Length = 67.0335
  MakeFace = true
  Placement = pos=(92.0028,73.817,-125.386) rot=(1,0,0;3.14159rad)
  Points = (2) [(0,0,0),(-67.0335,0.00403988,-1.42109e-14)]
  Start = (92.0028,73.817,-125.386)
  Subdivisions = 0
FEATURE [App::DocumentObjectGroup] Draft_Construction  label="Construction"
  Group = -> [Line328,Line329,Line330]
FEATURE [Part::Feature] Fusion002009002005002004028003007012002019001002001013004001001
  shape: bbox 48.16 x 37.82 x 3.8 mm, 89 faces (baked)
FEATURE [Part::Feature] Fusion002009002005002004028003007012002019001002001013004001010001001
  Placement = pos=(33.8842,-152.051,195.2) rot=(0,0,1;0rad)
  shape: bbox 59.49 x 46.04 x 199 mm, 49 faces (baked)
